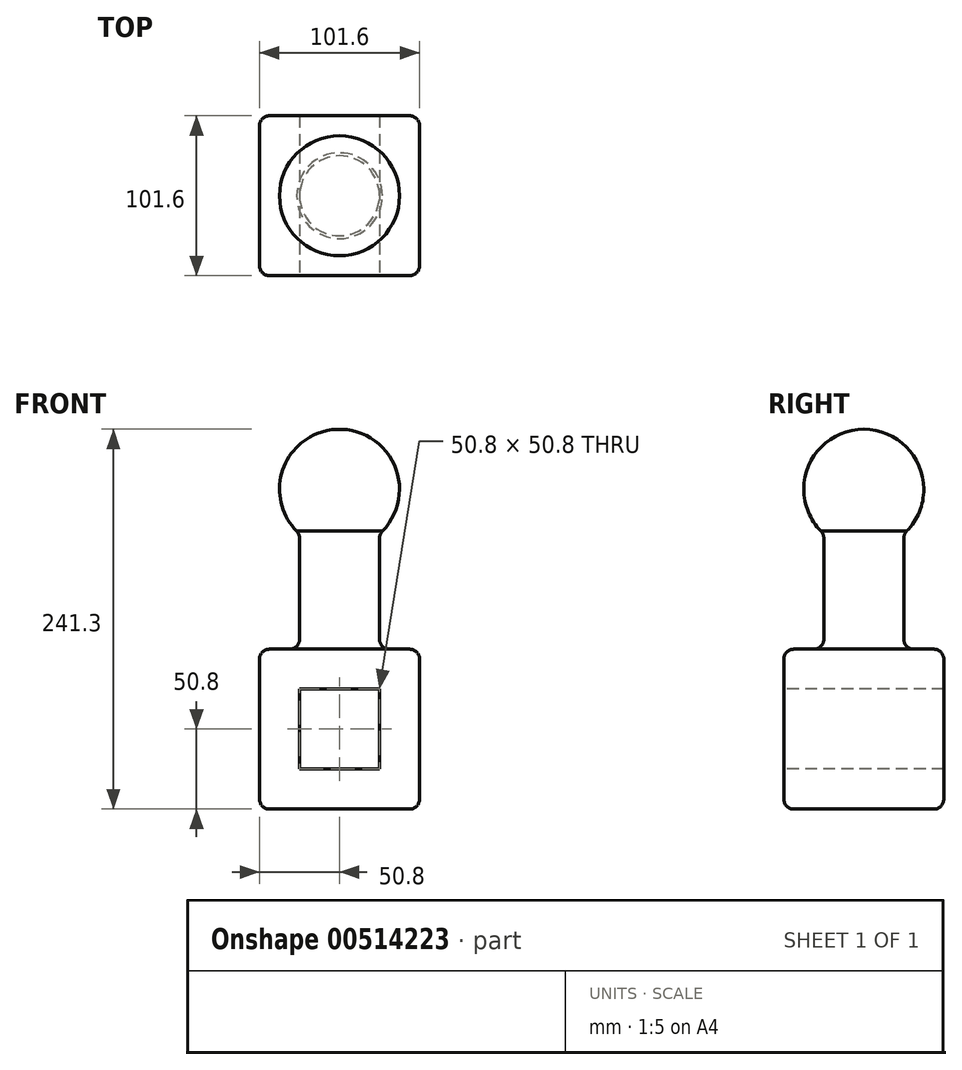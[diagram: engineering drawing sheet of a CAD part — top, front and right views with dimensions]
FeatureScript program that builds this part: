
annotation { "Feature Type Name" : "Feature", "Feature Type Description" : "" }
export const myFeature = defineFeature(function(context is Context, id is Id, definition is map)
    precondition{}
    {
        {
            var Q0;
            Q0=qCreatedBy(makeId("Top.planeOp"),FACE);
            var sketch = newSketch(context, id + "F0", { "sketchPlane" : qUnion([Q0])});
            skLineSegment(sketch, "E0.bottom", {"start": v(50.8, 50.8) * mm, "end": v(-50.8, 50.8) * mm});
            skLineSegment(sketch, "E0.top", {"start": v(50.8, -50.8) * mm, "end": v(-50.8, -50.8) * mm});
            skLineSegment(sketch, "E0.left", {"start": v(50.8, 50.8) * mm, "end": v(50.8, -50.8) * mm});
            skLineSegment(sketch, "E0.right", {"start": v(-50.8, 50.8) * mm, "end": v(-50.8, -50.8) * mm});
            skPoint(sketch, "E0.middle", {"position": v(0, 0) * mm});
            skSolve(sketch);
        }
        {
            var Q0;
            Q0 = qSketchRegion(id + "F0", true);
            extrude(context, id + "F1", {"entities" : qUnion([Q0]), "depth" : 101.6 * mm, "offsetDistance" : 25.4 * mm});
        }
        {
            var Q0;
            Q0=qCreatedBy(makeId("Top.planeOp"),FACE);
            var sketch = newSketch(context, id + "F2", { "sketchPlane" : qUnion([Q0])});
            skCircle(sketch, "E1", {"center": v(0, 0) * mm, "radius": 25.4 * mm});
            skSolve(sketch);
        }
        {
            var Q0;
            Q0 = qSketchRegion(id + "F2", true);
            extrude(context, id + "F3", {"entities" : qUnion([Q0]), "operationType" : NewBodyOperationType.ADD, "depth" : 203.2 * mm, "offsetDistance" : 25.4 * mm});
        }
        {
            var Q0;
            Q0=makeQuery(id+"F3.opExtrude","CAP_FACE",FACE,{"disambiguationData":[OSD([sQuery(id+"F2.wireOp",EDGE,"E1")])],"isStart":false});
            var sketch = newSketch(context, id + "F4", { "sketchPlane" : qUnion([Q0])});
            skArc(sketch, "E2", {"start": v(0, -38.1) * mm, "mid": v(38.1, 0) * mm, "end": v(0, 38.1) * mm});
            skLineSegment(sketch, "E3", {"start": v(0, 38.1) * mm, "end": v(0, -38.1) * mm});
            skSolve(sketch);
        }
        {
            var Q0;
            {var subQ0=sQuery(id+"F4.wireOp",EDGE,"E2");Q0=makeQuery(id+"F4.imprint","IMPRINT",FACE,{"disambiguationData":[TD([[makeQuery(id+"F4.imprint","IMPRINT",EDGE,{"derivedFrom":subQ0}),1.0]])]});}
            var Q1;
            {var subQ0=sQuery(id+"F4.wireOp",EDGE,"E3");var subQ1=makeQuery(id+"F3.opExtrude","CAP_EDGE",EDGE,{"disambiguationData":[OSD([sQuery(id+"F2.wireOp",EDGE,"E1")])],"isStart":false});var subQ2=makeQuery(id+"F4.imprint","INTERSECT",VERTEX,{"disambiguationData":[OD(0.0)],"derivedFrom":[subQ1,subQ0]});Q1=makeQuery(id+"F4.imprint","IMPRINT",FACE,{"disambiguationData":[TD([[makeQuery(id+"F4.imprint","IMPRINT",EDGE,{"disambiguationData":[TD([[subQ2,-1.0]])],"derivedFrom":subQ0}),1.0]])]});}
            var Q2;
            Q2=sQuery(id+"F4.wireOp",EDGE,"E3");
            revolve(context, id + "F5", {"operationType" : NewBodyOperationType.ADD, "entities" : qUnion([Q0, Q1]), "axis" : qUnion([Q2]), "revolveType" : RevolveType.FULL});
        }
        {
            var Q0;
            Q0=makeQuery(id+"F1.opExtrude","SWEPT_FACE",FACE,{"disambiguationData":[OSD([sQuery(id+"F0.wireOp",EDGE,"E0.top")])]});
            var sketch = newSketch(context, id + "F6", { "sketchPlane" : qUnion([Q0])});
            skLineSegment(sketch, "E4.bottom", {"start": v(25.4, 25.4) * mm, "end": v(-25.4, 25.4) * mm});
            skLineSegment(sketch, "E4.top", {"start": v(25.4, 76.2) * mm, "end": v(-25.4, 76.2) * mm});
            skLineSegment(sketch, "E4.left", {"start": v(25.4, 25.4) * mm, "end": v(25.4, 76.2) * mm});
            skLineSegment(sketch, "E4.right", {"start": v(-25.4, 25.4) * mm, "end": v(-25.4, 76.2) * mm});
            skPoint(sketch, "E4.middle", {"position": v(0, 50.8) * mm});
            skPoint(sketch, "E4.middle.positionSnap0", {"position": v(50.8, 50.8) * mm});
            skPoint(sketch, "E4.centerSnap0", {"position": v(50.8, 50.8) * mm});
            skSolve(sketch);
        }
        {
            var Q0;
            Q0 = qSketchRegion(id + "F6", true);
            extrude(context, id + "F7", {"entities" : qUnion([Q0]), "operationType" : NewBodyOperationType.REMOVE, "oppositeDirection" : true, "depth" : 101.6 * mm, "offsetDistance" : 25.4 * mm});
        }
        {
            var Q0;
            Q0=makeQuery(id+"F3.boolean.opBoolean","INTERSECT",EDGE,{"derivedFrom":[makeQuery(id+"F1.opExtrude","CAP_FACE",FACE,{"disambiguationData":[OSD([sQuery(id+"F0.wireOp",EDGE,"E0.bottom"),sQuery(id+"F0.wireOp",EDGE,"E0.top"),sQuery(id+"F0.wireOp",EDGE,"E0.left"),sQuery(id+"F0.wireOp",EDGE,"E0.right")])],"isStart":false}),makeQuery(id+"F3.opExtrude","SWEPT_FACE",FACE,{"disambiguationData":[OSD([sQuery(id+"F2.wireOp",EDGE,"E1")])]})]});
            var Q1;
            Q1=makeQuery(id+"F1.opExtrude","CAP_EDGE",EDGE,{"disambiguationData":[OSD([sQuery(id+"F0.wireOp",EDGE,"E0.left")])],"isStart":false});
            var Q2;
            Q2=makeQuery(id+"F1.opExtrude","SWEPT_EDGE",EDGE,{"disambiguationData":[OSD([sQuery(id+"F0.wireOp",EDGE,"E0.top"),sQuery(id+"F0.wireOp",EDGE,"E0.left")])]});
            var Q3;
            Q3=makeQuery(id+"F1.opExtrude","CAP_EDGE",EDGE,{"disambiguationData":[OSD([sQuery(id+"F0.wireOp",EDGE,"E0.top")])],"isStart":false});
            var Q4;
            Q4=makeQuery(id+"F1.opExtrude","CAP_EDGE",EDGE,{"disambiguationData":[OSD([sQuery(id+"F0.wireOp",EDGE,"E0.bottom")])],"isStart":false});
            var Q5;
            Q5=makeQuery(id+"F1.opExtrude","CAP_EDGE",EDGE,{"disambiguationData":[OSD([sQuery(id+"F0.wireOp",EDGE,"E0.right")])],"isStart":false});
            var Q6;
            Q6=makeQuery(id+"F5.boolean.opBoolean","INTERSECT",EDGE,{"derivedFrom":[makeQuery(id+"F3.opExtrude","SWEPT_FACE",FACE,{"disambiguationData":[OSD([sQuery(id+"F2.wireOp",EDGE,"E1")])]}),makeQuery(id+"F5.opRevolve","SWEPT_FACE",FACE,{"disambiguationData":[OSD([sQuery(id+"F4.wireOp",EDGE,"E2")])]})]});
            var Q7;
            Q7=makeQuery(id+"F1.opExtrude","SWEPT_EDGE",EDGE,{"disambiguationData":[OSD([sQuery(id+"F0.wireOp",EDGE,"E0.bottom"),sQuery(id+"F0.wireOp",EDGE,"E0.left")])]});
            var Q8;
            Q8=makeQuery(id+"F1.opExtrude","CAP_EDGE",EDGE,{"disambiguationData":[OSD([sQuery(id+"F0.wireOp",EDGE,"E0.left")])],"isStart":true});
            var Q9;
            Q9=makeQuery(id+"F1.opExtrude","CAP_EDGE",EDGE,{"disambiguationData":[OSD([sQuery(id+"F0.wireOp",EDGE,"E0.top")])],"isStart":true});
            var Q10;
            Q10=makeQuery(id+"F1.opExtrude","SWEPT_EDGE",EDGE,{"disambiguationData":[OSD([sQuery(id+"F0.wireOp",EDGE,"E0.top"),sQuery(id+"F0.wireOp",EDGE,"E0.right")])]});
            var Q11;
            Q11=makeQuery(id+"F1.opExtrude","SWEPT_EDGE",EDGE,{"disambiguationData":[OSD([sQuery(id+"F0.wireOp",EDGE,"E0.bottom"),sQuery(id+"F0.wireOp",EDGE,"E0.right")])]});
            var Q12;
            Q12=makeQuery(id+"F1.opExtrude","CAP_EDGE",EDGE,{"disambiguationData":[OSD([sQuery(id+"F0.wireOp",EDGE,"E0.bottom")])],"isStart":true});
            var Q13;
            Q13=makeQuery(id+"F1.opExtrude","CAP_EDGE",EDGE,{"disambiguationData":[OSD([sQuery(id+"F0.wireOp",EDGE,"E0.right")])],"isStart":true});
            fillet(context, id + "F8", {"entities" : qUnion([Q0, Q1, Q2, Q3, Q4, Q5, Q6, Q7, Q8, Q9, Q10, Q11, Q12, Q13]), "radius" : 6.35 * mm, "tangentPropagation" : true, "allowEdgeOverflow" : false});
        }
    });
